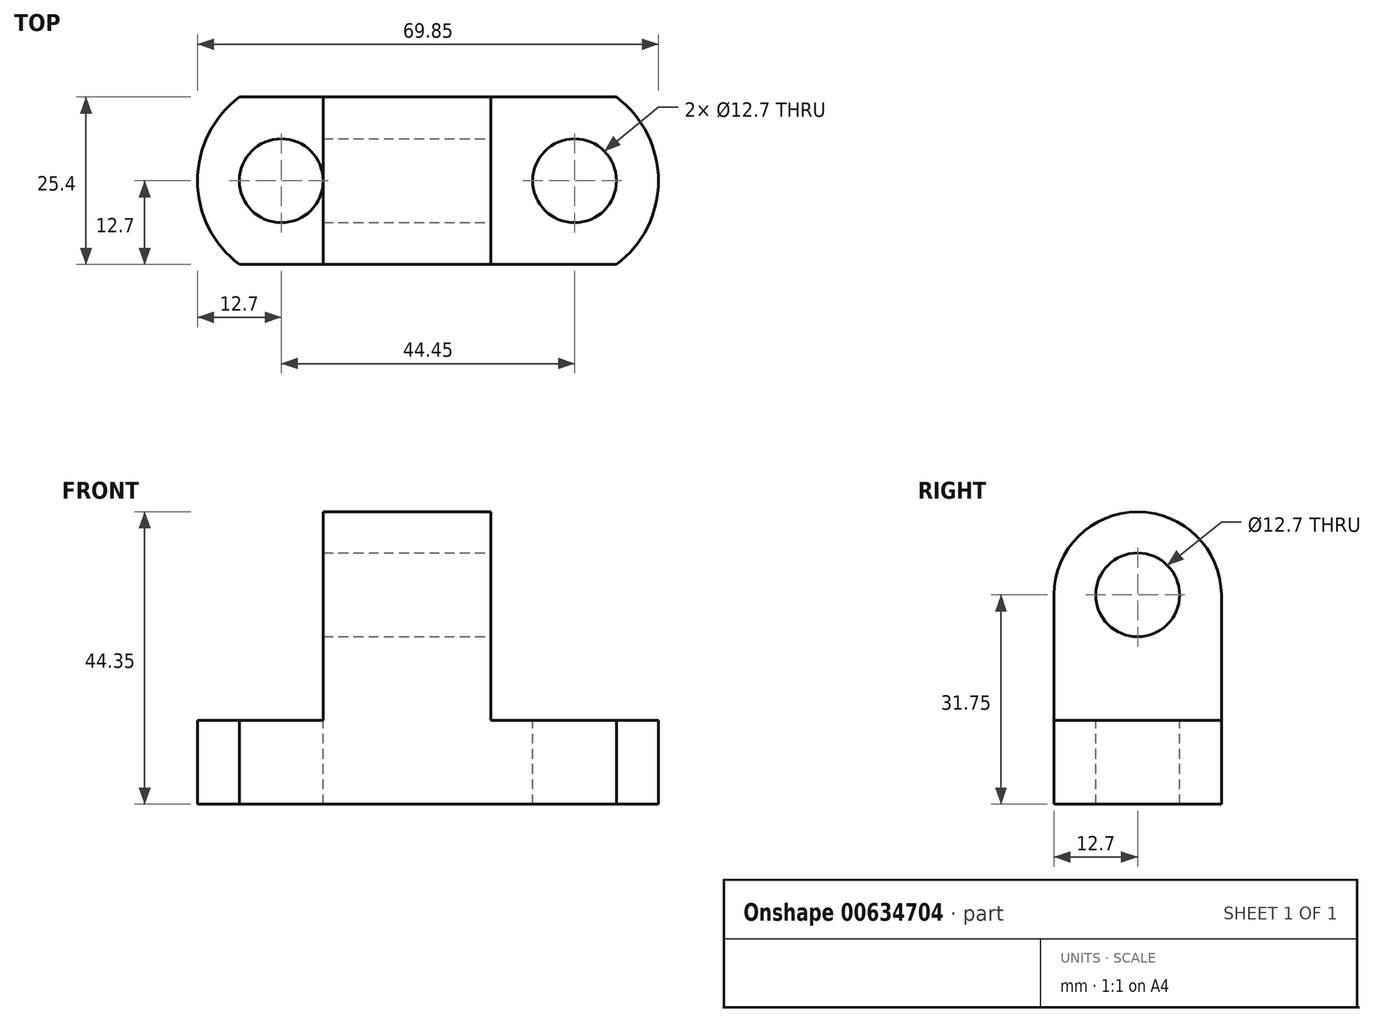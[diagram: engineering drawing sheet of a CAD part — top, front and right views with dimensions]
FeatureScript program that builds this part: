
annotation { "Feature Type Name" : "Feature", "Feature Type Description" : "" }
export const myFeature = defineFeature(function(context is Context, id is Id, definition is map)
    precondition{}
    {
        {
            var Q0;
            Q0=qCreatedBy(makeId("Front.planeOp"),FACE);
            var sketch = newSketch(context, id + "F0", { "sketchPlane" : qUnion([Q0])});
            skLineSegment(sketch, "E0", {"start": v(0, 0) * mm, "end": v(69.85, 0) * mm});
            skLineSegment(sketch, "E1", {"start": v(69.85, 0) * mm, "end": v(69.85, 12.7) * mm});
            skLineSegment(sketch, "E2", {"start": v(69.85, 12.7) * mm, "end": v(44.45, 12.7) * mm});
            skLineSegment(sketch, "E3", {"start": v(44.45, 12.7) * mm, "end": v(44.45, 44.45) * mm});
            skLineSegment(sketch, "E4", {"start": v(44.45, 44.45) * mm, "end": v(19.05, 44.45) * mm});
            skLineSegment(sketch, "E5", {"start": v(19.05, 44.45) * mm, "end": v(19.05, 12.7) * mm});
            skLineSegment(sketch, "E6", {"start": v(19.05, 12.7) * mm, "end": v(0, 12.7) * mm});
            skLineSegment(sketch, "E7", {"start": v(0, 12.7) * mm, "end": v(0, 0) * mm});
            skSolve(sketch);
        }
        {
            var Q0;
            Q0=qSketchRegion(id+"F0",true);
            extrude(context, id + "F1", {"entities" : qUnion([Q0]), "depth" : 25.4 * mm, "offsetDistance" : 25.4 * mm});
        }
        {
            var Q0;
            Q0=makeQuery(id+"F1.opExtrude","SWEPT_FACE",FACE,{"disambiguationData":[OSD([sQuery(id+"F0.wireOp",EDGE,"E2")])]});
            var sketch = newSketch(context, id + "F2", { "sketchPlane" : qUnion([Q0])});
            skCircle(sketch, "E8", {"center": v(57.15, -12.7) * mm, "radius": 6.35 * mm});
            skPoint(sketch, "E8.centerSnap0", {"position": v(57.15, 0) * mm});
            skArc(sketch, "E9", {"start": v(63.5, -25.4) * mm, "mid": v(69.85, -12.7) * mm, "end": v(63.5, 0) * mm});
            skCircle(sketch, "E10", {"center": v(12.7, -12.7) * mm, "radius": 6.35 * mm});
            skSolve(sketch);
        }
        {
            var Q0;
            Q0=makeQuery(id+"F2.imprint","IMPRINT",FACE,{"disambiguationData":[TD([[makeQuery(id+"F2.imprint","IMPRINT",EDGE,{"derivedFrom":sQuery(id+"F2.wireOp",EDGE,"E10")}),1.0]])]});
            var Q1;
            Q1=makeQuery(id+"F2.imprint","IMPRINT",FACE,{"disambiguationData":[TD([[makeQuery(id+"F2.imprint","IMPRINT",EDGE,{"derivedFrom":sQuery(id+"F2.wireOp",EDGE,"E8")}),1.0]])]});
            var Q2;
            {var subQ0=sQuery(id+"F2.wireOp",EDGE,"E9");var subQ1=sQuery(id+"F0.wireOp",EDGE,"E2");var subQ2=makeQuery(id+"F1.opExtrude","CAP_EDGE",EDGE,{"disambiguationData":[OSD([subQ1])],"isStart":false});var subQ3=makeQuery(id+"F2.imprint","INTERSECT",VERTEX,{"derivedFrom":[subQ2,subQ0]});Q2=makeQuery(id+"F2.imprint","IMPRINT",FACE,{"disambiguationData":[TD([[makeQuery(id+"F2.imprint","IMPRINT",EDGE,{"disambiguationData":[TD([[subQ3,-1.0]])],"derivedFrom":subQ0}),-1.0]])]});}
            var Q3;
            {var subQ0=sQuery(id+"F2.wireOp",EDGE,"E9");var subQ1=sQuery(id+"F0.wireOp",EDGE,"E2");var subQ2=makeQuery(id+"F1.opExtrude","CAP_EDGE",EDGE,{"disambiguationData":[OSD([subQ1])],"isStart":true});var subQ3=makeQuery(id+"F2.imprint","INTERSECT",VERTEX,{"derivedFrom":[subQ2,subQ0]});Q3=makeQuery(id+"F2.imprint","IMPRINT",FACE,{"disambiguationData":[TD([[makeQuery(id+"F2.imprint","IMPRINT",EDGE,{"disambiguationData":[TD([[subQ3,1.0]])],"derivedFrom":subQ0}),-1.0]])]});}
            extrude(context, id + "F3", {"entities" : qUnion([Q0, Q1, Q2, Q3]), "operationType" : NewBodyOperationType.REMOVE, "oppositeDirection" : true, "depth" : 25.4 * mm, "offsetDistance" : 25.4 * mm});
        }
        {
            var Q0;
            Q0=makeQuery(id+"F1.opExtrude","SWEPT_FACE",FACE,{"disambiguationData":[OSD([sQuery(id+"F0.wireOp",EDGE,"E6")])]});
            var sketch = newSketch(context, id + "F4", { "sketchPlane" : qUnion([Q0])});
            skArc(sketch, "E11", {"start": v(6.35, 0) * mm, "mid": v(0, -12.7) * mm, "end": v(6.35, -25.4) * mm});
            skSolve(sketch);
        }
        {
            var Q0;
            {var subQ0=sQuery(id+"F4.wireOp",EDGE,"E11");var subQ1=sQuery(id+"F0.wireOp",EDGE,"E6");var subQ2=makeQuery(id+"F1.opExtrude","CAP_EDGE",EDGE,{"disambiguationData":[OSD([subQ1])],"isStart":true});var subQ3=makeQuery(id+"F4.imprint","INTERSECT",VERTEX,{"derivedFrom":[subQ2,subQ0]});Q0=makeQuery(id+"F4.imprint","IMPRINT",FACE,{"disambiguationData":[TD([[makeQuery(id+"F4.imprint","IMPRINT",EDGE,{"disambiguationData":[TD([[subQ3,-1.0]])],"derivedFrom":subQ0}),-1.0]])]});}
            var Q1;
            {var subQ0=sQuery(id+"F4.wireOp",EDGE,"E11");var subQ1=sQuery(id+"F0.wireOp",EDGE,"E6");var subQ2=makeQuery(id+"F1.opExtrude","CAP_EDGE",EDGE,{"disambiguationData":[OSD([subQ1])],"isStart":false});var subQ3=makeQuery(id+"F4.imprint","INTERSECT",VERTEX,{"derivedFrom":[subQ2,subQ0]});Q1=makeQuery(id+"F4.imprint","IMPRINT",FACE,{"disambiguationData":[TD([[makeQuery(id+"F4.imprint","IMPRINT",EDGE,{"disambiguationData":[TD([[subQ3,1.0]])],"derivedFrom":subQ0}),-1.0]])]});}
            extrude(context, id + "F5", {"entities" : qUnion([Q0, Q1]), "operationType" : NewBodyOperationType.REMOVE, "oppositeDirection" : true, "depth" : 25.4 * mm, "offsetDistance" : 25.4 * mm});
        }
        {
            var Q0;
            Q0=makeQuery(id+"F1.opExtrude","SWEPT_FACE",FACE,{"disambiguationData":[OSD([sQuery(id+"F0.wireOp",EDGE,"E3")])]});
            var sketch = newSketch(context, id + "F6", { "sketchPlane" : qUnion([Q0])});
            skCircle(sketch, "E12", {"center": v(-12.7, 31.75) * mm, "radius": 6.35 * mm});
            skArc(sketch, "E13", {"start": v(0, 31.75) * mm, "mid": v(-12.7, 44.35) * mm, "end": v(-25.4, 31.75) * mm});
            skSolve(sketch);
        }
        {
            var Q0;
            {var subQ0=sQuery(id+"F6.wireOp",EDGE,"E13");Q0=makeQuery(id+"F6.imprint","IMPRINT",FACE,{"disambiguationData":[TD([[makeQuery(id+"F6.imprint","IMPRINT",EDGE,{"derivedFrom":subQ0}),-1.0]])]});}
            var Q1;
            Q1=makeQuery(id+"F6.imprint","IMPRINT",FACE,{"disambiguationData":[TD([[makeQuery(id+"F6.imprint","IMPRINT",EDGE,{"derivedFrom":sQuery(id+"F6.wireOp",EDGE,"E12")}),1.0]])]});
            extrude(context, id + "F7", {"entities" : qUnion([Q0, Q1]), "operationType" : NewBodyOperationType.REMOVE, "oppositeDirection" : true, "depth" : 25.4 * mm, "offsetDistance" : 25.4 * mm});
        }
    });
